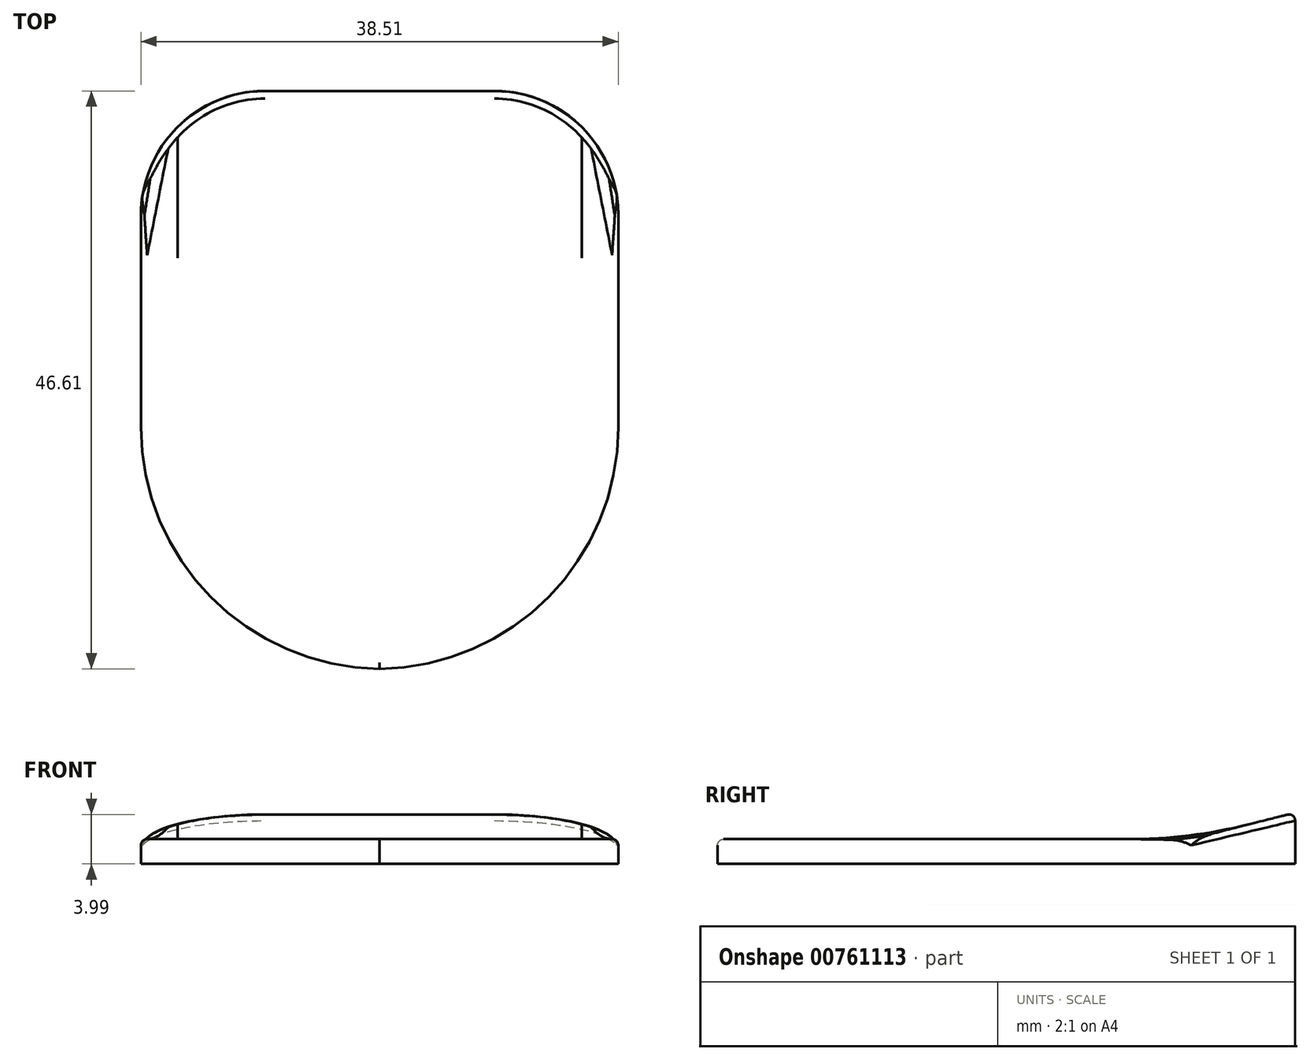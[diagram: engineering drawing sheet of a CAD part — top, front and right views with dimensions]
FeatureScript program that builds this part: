
annotation { "Feature Type Name" : "Feature", "Feature Type Description" : "" }
export const myFeature = defineFeature(function(context is Context, id is Id, definition is map)
    precondition{}
    {
        {
            var Q0;
            Q0=qCreatedBy(makeId("Top.planeOp"),FACE);
            var sketch = newSketch(context, id + "F0", { "sketchPlane" : qUnion([Q0])});
            skLineSegment(sketch, "E0.bottom", {"start": v(0, 0) * mm, "end": v(38.51, 0) * mm});
            skLineSegment(sketch, "E0.top", {"start": v(0, -46.61) * mm, "end": v(38.51, -46.61) * mm});
            skLineSegment(sketch, "E0.left", {"start": v(0, 0) * mm, "end": v(0, -46.61) * mm});
            skLineSegment(sketch, "E0.right", {"start": v(38.51, 0) * mm, "end": v(38.51, -46.61) * mm});
            skSolve(sketch);
        }
        {
            var Q0;
            Q0 = qSketchRegion(id + "F0", true);
            extrude(context, id + "F1", {"entities" : qUnion([Q0]), "depth" : 2 * mm, "offsetDistance" : 25 * mm});
        }
        {
            var Q0;
            Q0=makeQuery(id+"F1.opExtrude","SWEPT_EDGE",EDGE,{"disambiguationData":[OSD([sQuery(id+"F0.wireOp",EDGE,"E0.top"),sQuery(id+"F0.wireOp",EDGE,"E0.left")])]});
            var Q1;
            Q1=makeQuery(id+"F1.opExtrude","SWEPT_EDGE",EDGE,{"disambiguationData":[OSD([sQuery(id+"F0.wireOp",EDGE,"E0.top"),sQuery(id+"F0.wireOp",EDGE,"E0.right")])]});
            fillet(context, id + "F2", {"entities" : qUnion([Q0, Q1]), "radius" : 19.5 * mm, "tangentPropagation" : true, "allowEdgeOverflow" : false});
        }
        {
            var Q0;
            Q0=makeQuery(id+"F1.opExtrude","CAP_FACE",FACE,{"disambiguationData":[OSD([sQuery(id+"F0.wireOp",EDGE,"E0.bottom"),sQuery(id+"F0.wireOp",EDGE,"E0.top"),sQuery(id+"F0.wireOp",EDGE,"E0.left"),sQuery(id+"F0.wireOp",EDGE,"E0.right")])],"isStart":false});
            var sketch = newSketch(context, id + "F3", { "sketchPlane" : qUnion([Q0])});
            skLineSegment(sketch, "E1.bottom", {"start": v(0, 0) * mm, "end": v(38.51, 0) * mm});
            skLineSegment(sketch, "E1.top", {"start": v(0, -8.54) * mm, "end": v(38.51, -8.54) * mm});
            skLineSegment(sketch, "E1.left", {"start": v(0, 0) * mm, "end": v(0, -8.54) * mm});
            skLineSegment(sketch, "E1.right", {"start": v(38.51, 0) * mm, "end": v(38.51, -8.54) * mm});
            skSolve(sketch);
        }
        {
            var Q0;
            Q0 = qSketchRegion(id + "F3", true);
            extrude(context, id + "F4", {"entities" : qUnion([Q0]), "operationType" : NewBodyOperationType.ADD, "depth" : 2 * mm, "offsetDistance" : 25 * mm});
        }
        {
            var Q0;
            Q0=makeQuery(id+"F4.opExtrude","CAP_EDGE",EDGE,{"disambiguationData":[OSD([sQuery(id+"F3.wireOp",EDGE,"E1.top")])],"isStart":false});
            chamfer(context, id + "F5", {"entities" : qUnion([Q0]), "chamferType" : ChamferType.TWO_OFFSETS, "width1" : 8 * mm, "oppositeDirection" : false, "width2" : 2 * mm, "tangentPropagation" : true});
        }
        {
            var Q0;
            Q0=makeQuery(id+"F4.boolean.opBoolean","MERGE",EDGE,{"derivedFrom":[makeQuery(id+"F1.opExtrude","SWEPT_EDGE",EDGE,{"disambiguationData":[OSD([sQuery(id+"F0.wireOp",EDGE,"E0.bottom"),sQuery(id+"F0.wireOp",EDGE,"E0.left")])]}),makeQuery(id+"F4.opExtrude","SWEPT_EDGE",EDGE,{"disambiguationData":[OSD([sQuery(id+"F3.wireOp",EDGE,"E1.bottom"),sQuery(id+"F3.wireOp",EDGE,"E1.left")])]})]});
            var Q1;
            Q1=makeQuery(id+"F4.boolean.opBoolean","MERGE",EDGE,{"derivedFrom":[makeQuery(id+"F1.opExtrude","SWEPT_EDGE",EDGE,{"disambiguationData":[OSD([sQuery(id+"F0.wireOp",EDGE,"E0.bottom"),sQuery(id+"F0.wireOp",EDGE,"E0.right")])]}),makeQuery(id+"F4.opExtrude","SWEPT_EDGE",EDGE,{"disambiguationData":[OSD([sQuery(id+"F3.wireOp",EDGE,"E1.bottom"),sQuery(id+"F3.wireOp",EDGE,"E1.right")])]})]});
            fillet(context, id + "F6", {"entities" : qUnion([Q0, Q1]), "radius" : 10 * mm, "tangentPropagation" : true, "allowEdgeOverflow" : false});
        }
        {
            var Q0;
            {var subQ0=sQuery(id+"F0.wireOp",EDGE,"E0.right");var subQ1=sQuery(id+"F0.wireOp",EDGE,"E0.top");Q0=makeQuery(id+"F2.opFillet","BLEND_EDGE",EDGE,{"blendedFrom":[makeQuery(id+"F1.opExtrude","SWEPT_EDGE",EDGE,{"disambiguationData":[OSD([subQ1,subQ0])]}),makeQuery(id+"F1.opExtrude","CAP_FACE",FACE,{"disambiguationData":[OSD([sQuery(id+"F0.wireOp",EDGE,"E0.bottom"),subQ1,sQuery(id+"F0.wireOp",EDGE,"E0.left"),subQ0])],"isStart":false})],"blendedInto":[makeQuery(id+"F1.opExtrude","CAP_FACE",FACE,{"disambiguationData":[OSD([sQuery(id+"F0.wireOp",EDGE,"E0.bottom"),subQ1,sQuery(id+"F0.wireOp",EDGE,"E0.left"),subQ0])],"isStart":false})]});}
            var Q1;
            Q1=makeQuery(id+"F1.opExtrude","CAP_EDGE",EDGE,{"disambiguationData":[OSD([sQuery(id+"F0.wireOp",EDGE,"E0.right")])],"isStart":false});
            var Q2;
            {var subQ0=sQuery(id+"F0.wireOp",EDGE,"E0.left");var subQ1=sQuery(id+"F0.wireOp",EDGE,"E0.top");Q2=makeQuery(id+"F2.opFillet","BLEND_EDGE",EDGE,{"blendedFrom":[makeQuery(id+"F1.opExtrude","SWEPT_EDGE",EDGE,{"disambiguationData":[OSD([subQ1,subQ0])]}),makeQuery(id+"F1.opExtrude","CAP_FACE",FACE,{"disambiguationData":[OSD([sQuery(id+"F0.wireOp",EDGE,"E0.bottom"),subQ1,subQ0,sQuery(id+"F0.wireOp",EDGE,"E0.right")])],"isStart":false})],"blendedInto":[makeQuery(id+"F1.opExtrude","CAP_FACE",FACE,{"disambiguationData":[OSD([sQuery(id+"F0.wireOp",EDGE,"E0.bottom"),subQ1,subQ0,sQuery(id+"F0.wireOp",EDGE,"E0.right")])],"isStart":false})]});}
            var Q3;
            Q3=makeQuery(id+"F6.opFillet","BLEND_EDGE",EDGE,{"blendedFrom":[makeQuery(id+"F4.boolean.opBoolean","MERGE",EDGE,{"derivedFrom":[makeQuery(id+"F1.opExtrude","SWEPT_EDGE",EDGE,{"disambiguationData":[OSD([sQuery(id+"F0.wireOp",EDGE,"E0.bottom"),sQuery(id+"F0.wireOp",EDGE,"E0.left")])]}),makeQuery(id+"F4.opExtrude","SWEPT_EDGE",EDGE,{"disambiguationData":[OSD([sQuery(id+"F3.wireOp",EDGE,"E1.bottom"),sQuery(id+"F3.wireOp",EDGE,"E1.left")])]})]}),makeQuery(id+"F5.opChamfer","BLEND_FACE",FACE,{"disambiguationData":[OSD([sQuery(id+"F3.wireOp",EDGE,"E1.top")])]})],"blendedInto":[makeQuery(id+"F5.opChamfer","BLEND_FACE",FACE,{"disambiguationData":[OSD([sQuery(id+"F3.wireOp",EDGE,"E1.top")])]})]});
            var Q4;
            Q4=makeQuery(id+"F6.opFillet","BLEND_EDGE",EDGE,{"blendedFrom":[makeQuery(id+"F4.boolean.opBoolean","MERGE",EDGE,{"derivedFrom":[makeQuery(id+"F1.opExtrude","SWEPT_EDGE",EDGE,{"disambiguationData":[OSD([sQuery(id+"F0.wireOp",EDGE,"E0.bottom"),sQuery(id+"F0.wireOp",EDGE,"E0.right")])]}),makeQuery(id+"F4.opExtrude","SWEPT_EDGE",EDGE,{"disambiguationData":[OSD([sQuery(id+"F3.wireOp",EDGE,"E1.bottom"),sQuery(id+"F3.wireOp",EDGE,"E1.right")])]})]}),makeQuery(id+"F5.opChamfer","BLEND_FACE",FACE,{"disambiguationData":[OSD([sQuery(id+"F3.wireOp",EDGE,"E1.top")])]})],"blendedInto":[makeQuery(id+"F5.opChamfer","BLEND_FACE",FACE,{"disambiguationData":[OSD([sQuery(id+"F3.wireOp",EDGE,"E1.top")])]})]});
            var Q5;
            Q5=makeQuery(id+"F1.opExtrude","CAP_EDGE",EDGE,{"disambiguationData":[OSD([sQuery(id+"F0.wireOp",EDGE,"E0.left")])],"isStart":false});
            fillet(context, id + "F7", {"entities" : qUnion([Q0, Q1, Q2, Q3, Q4, Q5]), "radius" : 0.5 * mm, "tangentPropagation" : true, "allowEdgeOverflow" : false});
        }
        {
            var Q0;
            Q0=makeQuery(id+"F5.opChamfer","BLEND_EDGE",EDGE,{"blendedFrom":[makeQuery(id+"F4.opExtrude","CAP_EDGE",EDGE,{"disambiguationData":[OSD([sQuery(id+"F3.wireOp",EDGE,"E1.top")])],"isStart":false}),makeQuery(id+"F1.opExtrude","CAP_FACE",FACE,{"disambiguationData":[OSD([sQuery(id+"F0.wireOp",EDGE,"E0.bottom"),sQuery(id+"F0.wireOp",EDGE,"E0.top"),sQuery(id+"F0.wireOp",EDGE,"E0.left"),sQuery(id+"F0.wireOp",EDGE,"E0.right")])],"isStart":false})],"blendedInto":[makeQuery(id+"F1.opExtrude","CAP_FACE",FACE,{"disambiguationData":[OSD([sQuery(id+"F0.wireOp",EDGE,"E0.bottom"),sQuery(id+"F0.wireOp",EDGE,"E0.top"),sQuery(id+"F0.wireOp",EDGE,"E0.left"),sQuery(id+"F0.wireOp",EDGE,"E0.right")])],"isStart":false})]});
            fillet(context, id + "F8", {"entities" : qUnion([Q0]), "radius" : 40 * mm, "tangentPropagation" : true, "allowEdgeOverflow" : false});
        }
    });
